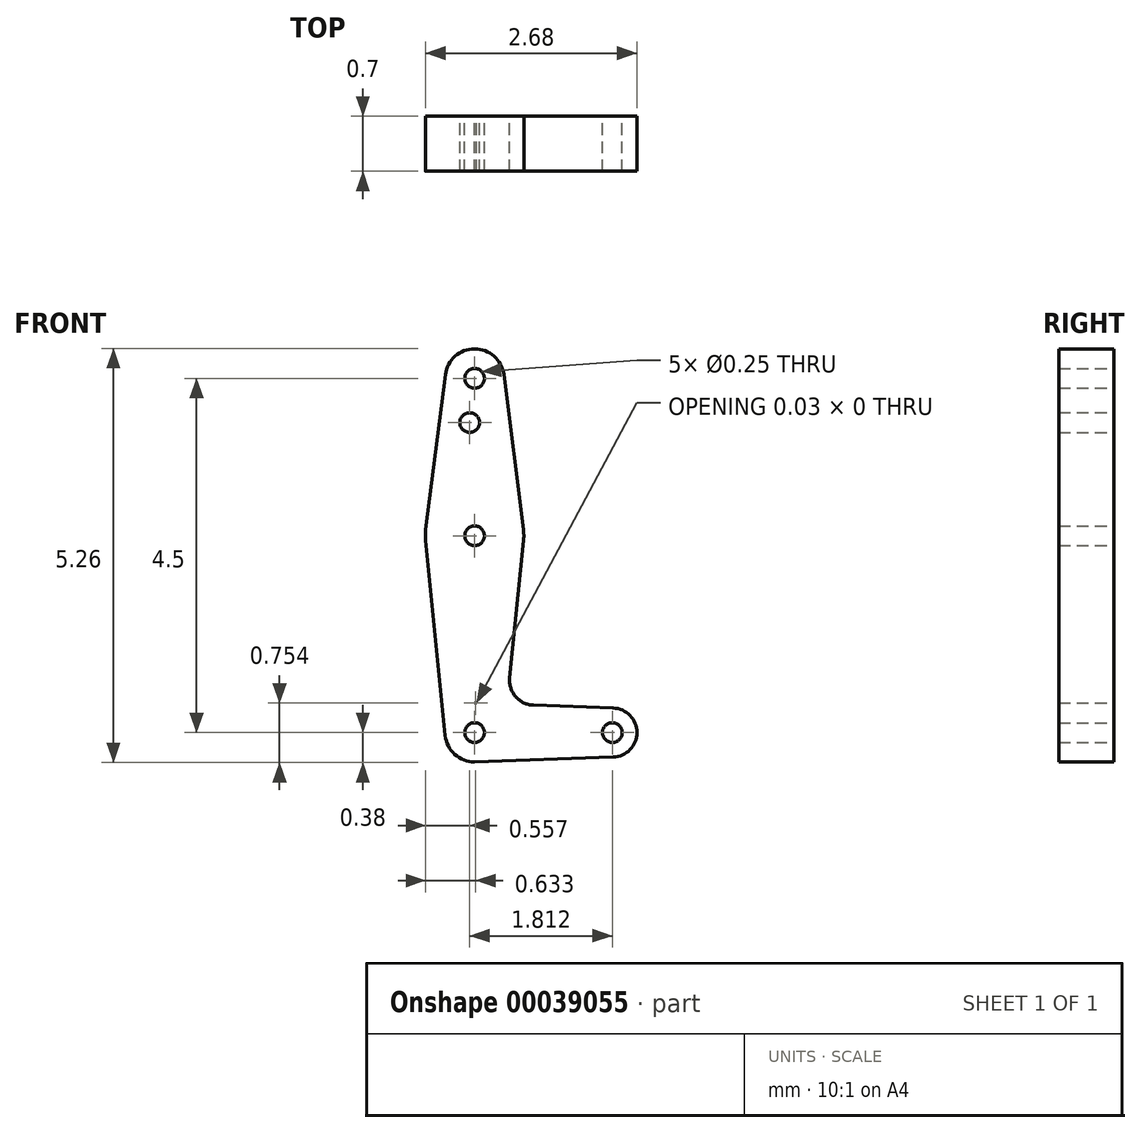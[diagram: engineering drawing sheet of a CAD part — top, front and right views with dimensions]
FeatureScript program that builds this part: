
annotation { "Feature Type Name" : "Feature", "Feature Type Description" : "" }
export const myFeature = defineFeature(function(context is Context, id is Id, definition is map)
    precondition{}
    {
        {
            var Q0;
            Q0=qCreatedBy(makeId("Front.planeOp"),FACE);
            var sketch = newSketch(context, id + "F0", { "sketchPlane" : qUnion([Q0])});
            skCircle(sketch, "E0", {"center": v(0, 0) * mm, "radius": 0.38 * mm});
            skLineSegment(sketch, "E1", {"start": v(0, 0) * mm, "end": v(0, 4.5) * mm, "construction": true});
            skCircle(sketch, "E2", {"center": v(0, 2.5) * mm, "radius": 0.63 * mm});
            skCircle(sketch, "E3", {"center": v(0, 4.5) * mm, "radius": 0.38 * mm});
            skLineSegment(sketch, "E4", {"start": v(0, 0) * mm, "end": v(1.75, 0) * mm, "construction": true});
            skCircle(sketch, "E5", {"center": v(1.75, 0) * mm, "radius": 0.31 * mm});
            skLineSegment(sketch, "E6", {"start": v(-0.37, 4.55) * mm, "end": v(-0.62, 2.58) * mm});
            skLineSegment(sketch, "E7", {"start": v(0.37, 4.55) * mm, "end": v(0.62, 2.58) * mm});
            skLineSegment(sketch, "E8", {"start": v(-0.62, 2.44) * mm, "end": v(-0.37, -0.04) * mm});
            skLineSegment(sketch, "E9", {"start": v(0.62, 2.44) * mm, "end": v(0.45, 0.7) * mm});
            skLineSegment(sketch, "E10", {"start": v(0, 0.37) * mm, "end": v(0.03, 0.37) * mm});
            skLineSegment(sketch, "E11", {"start": v(0, -0.37) * mm, "end": v(1.76, -0.31) * mm});
            skCircle(sketch, "E12", {"center": v(0, 4.5) * mm, "radius": 0.12 * mm});
            skCircle(sketch, "E13", {"center": v(0, 2.5) * mm, "radius": 0.12 * mm});
            skCircle(sketch, "E14", {"center": v(0, 0) * mm, "radius": 0.12 * mm});
            skCircle(sketch, "E15", {"center": v(1.75, 0) * mm, "radius": 0.12 * mm});
            skLineSegment(sketch, "E16.trimOffspring", {"start": v(0.75, 0.35) * mm, "end": v(1.76, 0.31) * mm});
            skLineSegment(sketch, "E17.trimOffspring", {"start": v(0.38, 0) * mm, "end": v(0.37, -0.04) * mm});
            skPoint(sketch, "E18.visualSharp", {"position": v(0.41, 0.36) * mm});
            skArc(sketch, "E18.filletArc", {"start": v(0.45, 0.7) * mm, "mid": v(0.52, 0.46) * mm, "end": v(0.75, 0.35) * mm});
            skCircle(sketch, "E19", {"center": v(-0.06, 3.94) * mm, "radius": 0.12 * mm});
            skSolve(sketch);
        }
        {
            var Q0;
            Q0=makeQuery(id+"F0.imprint","IMPRINT",FACE,{"disambiguationData":[TD([[makeQuery(id+"F0.imprint","IMPRINT",EDGE,{"derivedFrom":sQuery(id+"F0.wireOp",EDGE,"E12")}),-1.0]])]});
            var Q1;
            {var subQ2=sQuery(id+"F0.wireOp",EDGE,"E6");Q1=makeQuery(id+"F0.imprint","IMPRINT",FACE,{"disambiguationData":[TD([[makeQuery(id+"F0.imprint","IMPRINT",EDGE,{"derivedFrom":subQ2}),1.0]])]});}
            var Q2;
            Q2=makeQuery(id+"F0.imprint","IMPRINT",FACE,{"disambiguationData":[TD([[makeQuery(id+"F0.imprint","IMPRINT",EDGE,{"derivedFrom":sQuery(id+"F0.wireOp",EDGE,"E13")}),-1.0]])]});
            var Q3;
            {var subQ8=sQuery(id+"F0.wireOp",EDGE,"E8");Q3=makeQuery(id+"F0.imprint","IMPRINT",FACE,{"disambiguationData":[TD([[makeQuery(id+"F0.imprint","IMPRINT",EDGE,{"derivedFrom":subQ8}),1.0]])]});}
            var Q4;
            {var subQ4=sQuery(id+"F0.wireOp",EDGE,"E10");Q4=makeQuery(id+"F0.imprint","IMPRINT",FACE,{"disambiguationData":[TD([[makeQuery(id+"F0.imprint","IMPRINT",EDGE,{"derivedFrom":subQ4}),-1.0]])]});}
            var Q5;
            Q5=makeQuery(id+"F0.imprint","IMPRINT",FACE,{"disambiguationData":[TD([[makeQuery(id+"F0.imprint","IMPRINT",EDGE,{"derivedFrom":sQuery(id+"F0.wireOp",EDGE,"E15")}),-1.0]])]});
            extrude(context, id + "F1", {"entities" : qUnion([Q0, Q1, Q2, Q3, Q4, Q5]), "depth" : 0.7 * mm});
        }
    });
